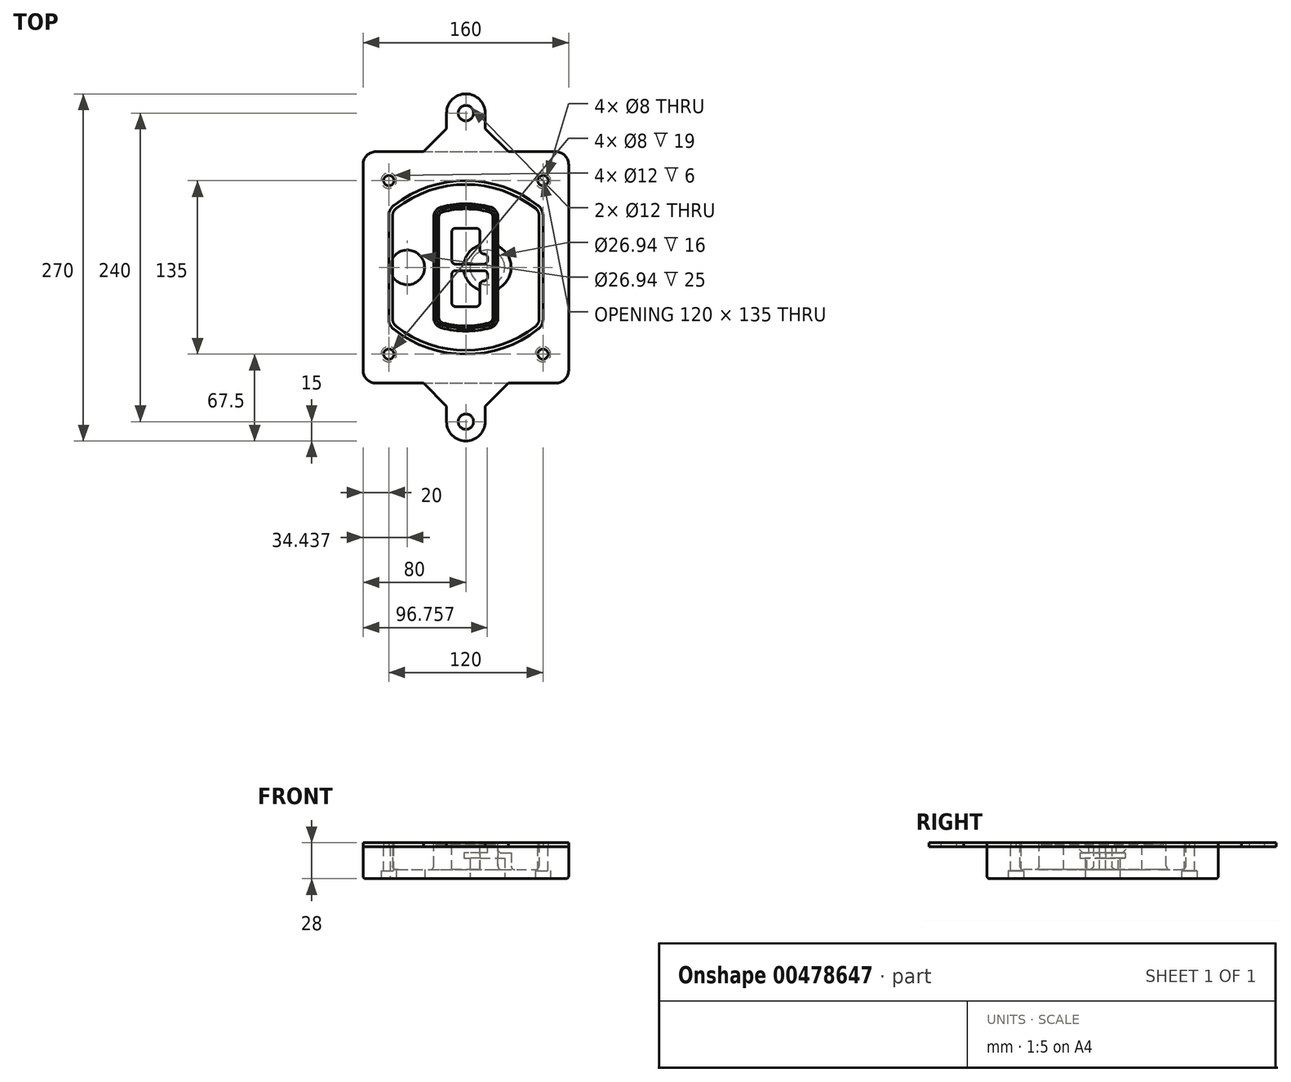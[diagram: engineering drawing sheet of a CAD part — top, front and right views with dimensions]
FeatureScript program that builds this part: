
annotation { "Feature Type Name" : "Feature", "Feature Type Description" : "" }
export const myFeature = defineFeature(function(context is Context, id is Id, definition is map)
    precondition{}
    {
        {
            var Q0;
            Q0=qCreatedBy(makeId("Top.planeOp"),FACE);
            var sketch = newSketch(context, id + "F0", { "sketchPlane" : qUnion([Q0])});
            skPoint(sketch, "E0.rect.middle", {"position": v(0, 0) * mm});
            skLineSegment(sketch, "E1.bottom", {"start": v(-70, -90) * mm, "end": v(70, -90) * mm});
            skLineSegment(sketch, "E1.top", {"start": v(-70, 90) * mm, "end": v(70, 90) * mm});
            skLineSegment(sketch, "E1.left", {"start": v(-80, -80) * mm, "end": v(-80, 80) * mm});
            skLineSegment(sketch, "E1.right", {"start": v(80, -80) * mm, "end": v(80, 80) * mm});
            skLineSegment(sketch, "E2", {"start": v(-80, 90) * mm, "end": v(80, -90) * mm, "construction": true});
            skLineSegment(sketch, "E3", {"start": v(80, 90) * mm, "end": v(-80, -90) * mm, "construction": true});
            skCircle(sketch, "E4", {"center": v(-60, 67.5) * mm, "radius": 4 * mm});
            skCircle(sketch, "E5", {"center": v(60, 67.5) * mm, "radius": 4 * mm});
            skCircle(sketch, "E6", {"center": v(60, -67.5) * mm, "radius": 4 * mm});
            skCircle(sketch, "E7", {"center": v(-60, -67.5) * mm, "radius": 4 * mm});
            skLineSegment(sketch, "E8", {"start": v(-60, 67.5) * mm, "end": v(60, 67.5) * mm, "construction": true});
            skLineSegment(sketch, "E9", {"start": v(60, 67.5) * mm, "end": v(60, -67.5) * mm, "construction": true});
            skLineSegment(sketch, "E10", {"start": v(60, -67.5) * mm, "end": v(-60, -67.5) * mm, "construction": true});
            skLineSegment(sketch, "E11", {"start": v(-60, -67.5) * mm, "end": v(-60, 67.5) * mm, "construction": true});
            skLineSegment(sketch, "E12", {"start": v(-60, 40.3) * mm, "end": v(-60, -40.3) * mm});
            skLineSegment(sketch, "E13", {"start": v(60, 40.3) * mm, "end": v(60, -40.3) * mm});
            skArc(sketch, "E14", {"start": v(56.15, 48.18) * mm, "mid": v(0, 67.5) * mm, "end": v(-56.15, 48.18) * mm});
            skArc(sketch, "E15", {"start": v(-56.15, -48.18) * mm, "mid": v(0, -67.5) * mm, "end": v(56.15, -48.18) * mm});
            skLineSegment(sketch, "E16", {"start": v(-60, 0) * mm, "end": v(60, 0) * mm, "construction": true});
            skPoint(sketch, "E17.visualSharp", {"position": v(-60, -45) * mm});
            skArc(sketch, "E17.filletArc", {"start": v(-60, -40.3) * mm, "mid": v(-58.99, -44.68) * mm, "end": v(-56.15, -48.18) * mm});
            skPoint(sketch, "E18.visualSharp", {"position": v(-60, 45) * mm});
            skArc(sketch, "E18.filletArc", {"start": v(-56.15, 48.18) * mm, "mid": v(-58.99, 44.68) * mm, "end": v(-60, 40.3) * mm});
            skPoint(sketch, "E19.visualSharp", {"position": v(60, 45) * mm});
            skArc(sketch, "E19.filletArc", {"start": v(60, 40.3) * mm, "mid": v(58.99, 44.68) * mm, "end": v(56.15, 48.18) * mm});
            skPoint(sketch, "E20.visualSharp", {"position": v(60, -45) * mm});
            skArc(sketch, "E20.filletArc", {"start": v(56.15, -48.18) * mm, "mid": v(58.99, -44.68) * mm, "end": v(60, -40.3) * mm});
            skPoint(sketch, "E21.visualSharp", {"position": v(-80, 90) * mm});
            skArc(sketch, "E21.filletArc", {"start": v(-70, 90) * mm, "mid": v(-77.07, 87.07) * mm, "end": v(-80, 80) * mm});
            skPoint(sketch, "E22.visualSharp", {"position": v(80, 90) * mm});
            skArc(sketch, "E22.filletArc", {"start": v(80, 80) * mm, "mid": v(77.07, 87.07) * mm, "end": v(70, 90) * mm});
            skPoint(sketch, "E23.visualSharp", {"position": v(80, -90) * mm});
            skArc(sketch, "E23.filletArc", {"start": v(70, -90) * mm, "mid": v(77.07, -87.07) * mm, "end": v(80, -80) * mm});
            skPoint(sketch, "E24.visualSharp", {"position": v(-80, -90) * mm});
            skArc(sketch, "E24.filletArc", {"start": v(-80, -80) * mm, "mid": v(-77.07, -87.07) * mm, "end": v(-70, -90) * mm});
            skArc(sketch, "E25.0", {"start": v(57, 40.3) * mm, "mid": v(56.3, 43.36) * mm, "end": v(54.3, 45.81) * mm});
            skLineSegment(sketch, "E25.1", {"start": v(57, 40.3) * mm, "end": v(57, -40.3) * mm});
            skArc(sketch, "E25.2", {"start": v(54.3, -45.81) * mm, "mid": v(56.3, -43.36) * mm, "end": v(57, -40.3) * mm});
            skArc(sketch, "E25.3", {"start": v(-54.3, -45.81) * mm, "mid": v(0, -64.5) * mm, "end": v(54.3, -45.81) * mm});
            skArc(sketch, "E25.4", {"start": v(-57, -40.3) * mm, "mid": v(-56.3, -43.36) * mm, "end": v(-54.3, -45.81) * mm});
            skArc(sketch, "E25.5", {"start": v(54.3, 45.81) * mm, "mid": v(0, 64.5) * mm, "end": v(-54.3, 45.81) * mm});
            skLineSegment(sketch, "E25.6", {"start": v(-57, 40.3) * mm, "end": v(-57, -40.3) * mm});
            skArc(sketch, "E25.7", {"start": v(-54.3, 45.81) * mm, "mid": v(-56.3, 43.36) * mm, "end": v(-57, 40.3) * mm});
            skArc(sketch, "E26.0", {"start": v(-58.62, 51.33) * mm, "mid": v(-62.58, 46.43) * mm, "end": v(-64, 40.3) * mm});
            skArc(sketch, "E26.1", {"start": v(58.62, 51.33) * mm, "mid": v(0, 71.5) * mm, "end": v(-58.62, 51.33) * mm});
            skArc(sketch, "E26.2", {"start": v(64, 40.3) * mm, "mid": v(62.58, 46.43) * mm, "end": v(58.62, 51.33) * mm});
            skLineSegment(sketch, "E26.3", {"start": v(64, 40.3) * mm, "end": v(64, -40.3) * mm});
            skArc(sketch, "E26.4", {"start": v(58.62, -51.33) * mm, "mid": v(62.58, -46.43) * mm, "end": v(64, -40.3) * mm});
            skLineSegment(sketch, "E26.5", {"start": v(-64, 40.3) * mm, "end": v(-64, -40.3) * mm});
            skArc(sketch, "E26.6", {"start": v(-58.62, -51.33) * mm, "mid": v(0, -71.5) * mm, "end": v(58.62, -51.33) * mm});
            skArc(sketch, "E26.7", {"start": v(-64, -40.3) * mm, "mid": v(-62.58, -46.43) * mm, "end": v(-58.62, -51.33) * mm});
            skSolve(sketch);
        }
        {
            var Q0;
            Q0=makeQuery(id+"F0.imprint","IMPRINT",FACE,{"disambiguationData":[TD([[makeQuery(id+"F0.imprint","IMPRINT",EDGE,{"derivedFrom":sQuery(id+"F0.wireOp",EDGE,"E1.bottom")}),1.0]])]});
            var Q1;
            Q1=makeQuery(id+"F0.imprint","IMPRINT",FACE,{"disambiguationData":[TD([[makeQuery(id+"F0.imprint","IMPRINT",EDGE,{"derivedFrom":sQuery(id+"F0.wireOp",EDGE,"E12")}),1.0]])]});
            var Q2;
            Q2=makeQuery(id+"F0.imprint","IMPRINT",FACE,{"disambiguationData":[TD([[makeQuery(id+"F0.imprint","IMPRINT",EDGE,{"derivedFrom":sQuery(id+"F0.wireOp",EDGE,"E25.0")}),1.0]])]});
            var Q3;
            Q3=makeQuery(id+"F0.imprint","IMPRINT",FACE,{"disambiguationData":[TD([[makeQuery(id+"F0.imprint","IMPRINT",EDGE,{"derivedFrom":sQuery(id+"F0.wireOp",EDGE,"E12")}),-1.0]])]});
            extrude(context, id + "F1", {"entities" : qUnion([Q0, Q1, Q2, Q3]), "oppositeDirection" : true, "depth" : 25 * mm});
        }
        {
            var Q0;
            Q0=makeQuery(id+"F0.imprint","IMPRINT",FACE,{"disambiguationData":[TD([[makeQuery(id+"F0.imprint","IMPRINT",EDGE,{"derivedFrom":sQuery(id+"F0.wireOp",EDGE,"E12")}),1.0]])]});
            extrude(context, id + "F2", {"entities" : qUnion([Q0]), "operationType" : NewBodyOperationType.ADD, "depth" : 3 * mm});
        }
        {
            var Q0;
            Q0=makeQuery(id+"F0.imprint","IMPRINT",FACE,{"disambiguationData":[TD([[makeQuery(id+"F0.imprint","IMPRINT",EDGE,{"derivedFrom":sQuery(id+"F0.wireOp",EDGE,"E25.0")}),1.0]])]});
            extrude(context, id + "F3", {"entities" : qUnion([Q0]), "operationType" : NewBodyOperationType.REMOVE, "oppositeDirection" : true, "depth" : 18 * mm});
        }
        {
            var Q0;
            Q0=makeQuery(id+"F2.opExtrude","CAP_FACE",FACE,{"disambiguationData":[OSD([sQuery(id+"F0.wireOp",EDGE,"E12"),sQuery(id+"F0.wireOp",EDGE,"E13"),sQuery(id+"F0.wireOp",EDGE,"E14"),sQuery(id+"F0.wireOp",EDGE,"E15"),sQuery(id+"F0.wireOp",EDGE,"E17.filletArc"),sQuery(id+"F0.wireOp",EDGE,"E18.filletArc"),sQuery(id+"F0.wireOp",EDGE,"E19.filletArc"),sQuery(id+"F0.wireOp",EDGE,"E20.filletArc"),sQuery(id+"F0.wireOp",EDGE,"E25.0"),sQuery(id+"F0.wireOp",EDGE,"E25.1"),sQuery(id+"F0.wireOp",EDGE,"E25.2"),sQuery(id+"F0.wireOp",EDGE,"E25.3"),sQuery(id+"F0.wireOp",EDGE,"E25.4"),sQuery(id+"F0.wireOp",EDGE,"E25.5"),sQuery(id+"F0.wireOp",EDGE,"E25.6"),sQuery(id+"F0.wireOp",EDGE,"E25.7")])],"isStart":false});
            var sketch = newSketch(context, id + "F4", { "sketchPlane" : qUnion([Q0])});
            skArc(sketch, "E27.0", {"start": v(-19.08, -46.97) * mm, "mid": v(0, -49.5) * mm, "end": v(19.08, -46.97) * mm});
            skArc(sketch, "E28.0", {"start": v(19.08, 46.97) * mm, "mid": v(0, 49.5) * mm, "end": v(-19.08, 46.97) * mm});
            skLineSegment(sketch, "E29", {"start": v(-25, 39.25) * mm, "end": v(-25, -39.25) * mm});
            skLineSegment(sketch, "E30", {"start": v(25, 39.25) * mm, "end": v(25, -39.25) * mm});
            skLineSegment(sketch, "E31", {"start": v(-25, 45.1) * mm, "end": v(25, 45.1) * mm, "construction": true});
            skLineSegment(sketch, "E32", {"start": v(-25, -45.1) * mm, "end": v(25, -45.1) * mm, "construction": true});
            skPoint(sketch, "E33.visualSharp", {"position": v(-25, 45.1) * mm});
            skArc(sketch, "E33.filletArc", {"start": v(-19.08, 46.97) * mm, "mid": v(-23.35, 44.11) * mm, "end": v(-25, 39.25) * mm});
            skPoint(sketch, "E34.visualSharp", {"position": v(25, 45.1) * mm});
            skArc(sketch, "E34.filletArc", {"start": v(25, 39.25) * mm, "mid": v(23.35, 44.11) * mm, "end": v(19.08, 46.97) * mm});
            skPoint(sketch, "E35.visualSharp", {"position": v(25, -45.1) * mm});
            skArc(sketch, "E35.filletArc", {"start": v(19.08, -46.97) * mm, "mid": v(23.35, -44.11) * mm, "end": v(25, -39.25) * mm});
            skPoint(sketch, "E36.visualSharp", {"position": v(-25, -45.1) * mm});
            skArc(sketch, "E36.filletArc", {"start": v(-25, -39.25) * mm, "mid": v(-23.35, -44.11) * mm, "end": v(-19.08, -46.97) * mm});
            skArc(sketch, "E37.0", {"start": v(54.3, 45.81) * mm, "mid": v(0, 64.5) * mm, "end": v(-54.3, 45.81) * mm});
            skArc(sketch, "E37.1", {"start": v(-54.3, 45.81) * mm, "mid": v(-56.3, 43.36) * mm, "end": v(-57, 40.3) * mm});
            skLineSegment(sketch, "E37.2", {"start": v(-57, 40.3) * mm, "end": v(-57, -40.3) * mm});
            skArc(sketch, "E37.3", {"start": v(-57, -40.3) * mm, "mid": v(-56.3, -43.36) * mm, "end": v(-54.3, -45.81) * mm});
            skArc(sketch, "E37.4", {"start": v(-54.3, -45.81) * mm, "mid": v(0, -64.5) * mm, "end": v(54.3, -45.81) * mm});
            skArc(sketch, "E37.5", {"start": v(54.3, -45.81) * mm, "mid": v(56.3, -43.36) * mm, "end": v(57, -40.3) * mm});
            skLineSegment(sketch, "E37.6", {"start": v(57, 40.3) * mm, "end": v(57, -40.3) * mm});
            skArc(sketch, "E37.7", {"start": v(57, 40.3) * mm, "mid": v(56.3, 43.36) * mm, "end": v(54.3, 45.81) * mm});
            skLineSegment(sketch, "E38.0", {"start": v(23, 39.25) * mm, "end": v(23, -39.25) * mm});
            skArc(sketch, "E38.1", {"start": v(18.56, -45.04) * mm, "mid": v(21.76, -42.9) * mm, "end": v(23, -39.25) * mm});
            skArc(sketch, "E38.2", {"start": v(-18.56, -45.04) * mm, "mid": v(0, -47.5) * mm, "end": v(18.56, -45.04) * mm});
            skArc(sketch, "E38.3", {"start": v(-23, -39.25) * mm, "mid": v(-21.76, -42.9) * mm, "end": v(-18.56, -45.04) * mm});
            skLineSegment(sketch, "E38.4", {"start": v(-23, 39.25) * mm, "end": v(-23, -39.25) * mm});
            skArc(sketch, "E38.5", {"start": v(23, 39.25) * mm, "mid": v(21.76, 42.9) * mm, "end": v(18.56, 45.04) * mm});
            skArc(sketch, "E38.6", {"start": v(-18.56, 45.04) * mm, "mid": v(-21.76, 42.9) * mm, "end": v(-23, 39.25) * mm});
            skArc(sketch, "E38.7", {"start": v(18.56, 45.04) * mm, "mid": v(0, 47.5) * mm, "end": v(-18.56, 45.04) * mm});
            skArc(sketch, "E39.0", {"start": v(21, 39.25) * mm, "mid": v(20.18, 41.68) * mm, "end": v(18.04, 43.1) * mm});
            skLineSegment(sketch, "E39.1", {"start": v(21, 39.25) * mm, "end": v(21, -39.25) * mm});
            skArc(sketch, "E39.2", {"start": v(18.04, -43.1) * mm, "mid": v(20.18, -41.68) * mm, "end": v(21, -39.25) * mm});
            skArc(sketch, "E39.3", {"start": v(-18.04, -43.1) * mm, "mid": v(0, -45.5) * mm, "end": v(18.04, -43.1) * mm});
            skArc(sketch, "E39.4", {"start": v(-21, -39.25) * mm, "mid": v(-20.18, -41.68) * mm, "end": v(-18.04, -43.1) * mm});
            skArc(sketch, "E39.5", {"start": v(18.04, 43.1) * mm, "mid": v(0, 45.5) * mm, "end": v(-18.04, 43.1) * mm});
            skLineSegment(sketch, "E39.6", {"start": v(-21, 39.25) * mm, "end": v(-21, -39.25) * mm});
            skArc(sketch, "E39.7", {"start": v(-18.04, 43.1) * mm, "mid": v(-20.18, 41.68) * mm, "end": v(-21, 39.25) * mm});
            skLineSegment(sketch, "E40", {"start": v(-25, 0) * mm, "end": v(25, 0) * mm, "construction": true});
            skLineSegment(sketch, "E41", {"start": v(-11, 5.5) * mm, "end": v(-11, 27.5) * mm});
            skLineSegment(sketch, "E42", {"start": v(-8, 30.5) * mm, "end": v(8, 30.5) * mm});
            skLineSegment(sketch, "E43", {"start": v(11, 27.5) * mm, "end": v(11, 13.5) * mm});
            skLineSegment(sketch, "E44", {"start": v(14, 10.5) * mm, "end": v(14, 10.5) * mm});
            skLineSegment(sketch, "E45", {"start": v(17, 7.5) * mm, "end": v(17, 5.5) * mm});
            skLineSegment(sketch, "E46", {"start": v(14, 2.5) * mm, "end": v(-8, 2.5) * mm});
            skPoint(sketch, "E47.visualSharp", {"position": v(-11, 30.5) * mm});
            skArc(sketch, "E47.filletArc", {"start": v(-8, 30.5) * mm, "mid": v(-10.12, 29.62) * mm, "end": v(-11, 27.5) * mm});
            skPoint(sketch, "E48.visualSharp", {"position": v(11, 30.5) * mm});
            skArc(sketch, "E48.filletArc", {"start": v(11, 27.5) * mm, "mid": v(10.12, 29.62) * mm, "end": v(8, 30.5) * mm});
            skPoint(sketch, "E49.visualSharp", {"position": v(11, 10.5) * mm});
            skArc(sketch, "E49.filletArc", {"start": v(11, 13.5) * mm, "mid": v(11.88, 11.38) * mm, "end": v(14, 10.5) * mm});
            skPoint(sketch, "E50.visualSharp", {"position": v(17, 10.5) * mm});
            skArc(sketch, "E50.filletArc", {"start": v(17, 7.5) * mm, "mid": v(16.12, 9.62) * mm, "end": v(14, 10.5) * mm});
            skPoint(sketch, "E51.visualSharp", {"position": v(17, 2.5) * mm});
            skArc(sketch, "E51.filletArc", {"start": v(14, 2.5) * mm, "mid": v(16.12, 3.38) * mm, "end": v(17, 5.5) * mm});
            skPoint(sketch, "E52.visualSharp", {"position": v(-11, 2.5) * mm});
            skArc(sketch, "E52.filletArc", {"start": v(-11, 5.5) * mm, "mid": v(-10.12, 3.38) * mm, "end": v(-8, 2.5) * mm});
            skLineSegment(sketch, "E53.0.MirrorCS", {"start": v(14, -2.5) * mm, "end": v(-8, -2.5) * mm});
            skArc(sketch, "E54.0.MirrorCS", {"start": v(-11, -5.5) * mm, "mid": v(-10.12, -3.38) * mm, "end": v(-8, -2.5) * mm});
            skLineSegment(sketch, "E55.0.MirrorCS", {"start": v(-11, -5.5) * mm, "end": v(-11, -27.5) * mm});
            skArc(sketch, "E56.0.MirrorCS", {"start": v(-8, -30.5) * mm, "mid": v(-10.12, -29.62) * mm, "end": v(-11, -27.5) * mm});
            skLineSegment(sketch, "E57.0.MirrorCS", {"start": v(-8, -30.5) * mm, "end": v(8, -30.5) * mm});
            skArc(sketch, "E58.0.MirrorCS", {"start": v(11, -27.5) * mm, "mid": v(10.12, -29.62) * mm, "end": v(8, -30.5) * mm});
            skLineSegment(sketch, "E59.0.MirrorCS", {"start": v(11, -27.5) * mm, "end": v(11, -13.5) * mm});
            skArc(sketch, "E60.0.MirrorCS", {"start": v(11, -13.5) * mm, "mid": v(11.88, -11.38) * mm, "end": v(14, -10.5) * mm});
            skArc(sketch, "E61.0.MirrorCS", {"start": v(17, -7.5) * mm, "mid": v(16.12, -9.62) * mm, "end": v(14, -10.5) * mm});
            skLineSegment(sketch, "E62.0.MirrorCS", {"start": v(17, -7.5) * mm, "end": v(17, -5.5) * mm});
            skArc(sketch, "E63.0.MirrorCS", {"start": v(14, -2.5) * mm, "mid": v(16.12, -3.38) * mm, "end": v(17, -5.5) * mm});
            skSolve(sketch);
        }
        {
            var Q0;
            Q0=makeQuery(id+"F4.imprint","IMPRINT",FACE,{"disambiguationData":[TD([[makeQuery(id+"F4.imprint","IMPRINT",EDGE,{"derivedFrom":sQuery(id+"F4.wireOp",EDGE,"E27.0")}),1.0]])]});
            var Q1;
            Q1=makeQuery(id+"F4.imprint","IMPRINT",FACE,{"disambiguationData":[TD([[makeQuery(id+"F4.imprint","IMPRINT",EDGE,{"derivedFrom":sQuery(id+"F4.wireOp",EDGE,"E38.0")}),-1.0]])]});
            var Q2;
            Q2=makeQuery(id+"F4.imprint","IMPRINT",FACE,{"disambiguationData":[TD([[makeQuery(id+"F4.imprint","IMPRINT",EDGE,{"derivedFrom":sQuery(id+"F4.wireOp",EDGE,"E39.0")}),1.0]])]});
            extrude(context, id + "F5", {"entities" : qUnion([Q0, Q1, Q2]), "operationType" : NewBodyOperationType.ADD, "endBound" : BoundingType.UP_TO_NEXT, "oppositeDirection" : true, "depth" : 25 * mm});
        }
        {
            var Q0;
            Q0=makeQuery(id+"F4.imprint","IMPRINT",FACE,{"disambiguationData":[TD([[makeQuery(id+"F4.imprint","IMPRINT",EDGE,{"derivedFrom":sQuery(id+"F4.wireOp",EDGE,"E38.0")}),-1.0]])]});
            extrude(context, id + "F6", {"entities" : qUnion([Q0]), "operationType" : NewBodyOperationType.REMOVE, "oppositeDirection" : true, "depth" : 2 * mm});
        }
        {
            var Q0;
            Q0=makeQuery(id+"F1.opExtrude","CAP_FACE",FACE,{"disambiguationData":[OSD([sQuery(id+"F0.wireOp",EDGE,"E1.bottom"),sQuery(id+"F0.wireOp",EDGE,"E1.top"),sQuery(id+"F0.wireOp",EDGE,"E1.left"),sQuery(id+"F0.wireOp",EDGE,"E1.right"),sQuery(id+"F0.wireOp",EDGE,"E4"),sQuery(id+"F0.wireOp",EDGE,"E5"),sQuery(id+"F0.wireOp",EDGE,"E6"),sQuery(id+"F0.wireOp",EDGE,"E7"),sQuery(id+"F0.wireOp",EDGE,"E21.filletArc"),sQuery(id+"F0.wireOp",EDGE,"E22.filletArc"),sQuery(id+"F0.wireOp",EDGE,"E23.filletArc"),sQuery(id+"F0.wireOp",EDGE,"E24.filletArc")])],"isStart":false});
            var sketch = newSketch(context, id + "F7", { "sketchPlane" : qUnion([Q0])});
            skCircle(sketch, "E64", {"center": v(16.76, 0) * mm, "radius": 13.47 * mm});
            skCircle(sketch, "E65", {"center": v(-45.56, 0) * mm, "radius": 13.47 * mm});
            skLineSegment(sketch, "E66", {"start": v(80, 0) * mm, "end": v(-80, 0) * mm});
            skCircle(sketch, "E67", {"center": v(16.76, 0) * mm, "radius": 18.47 * mm});
            skCircle(sketch, "E68", {"center": v(60, -67.5) * mm, "radius": 6 * mm});
            skCircle(sketch, "E69", {"center": v(-60, -67.5) * mm, "radius": 6 * mm});
            skCircle(sketch, "E70", {"center": v(-60, 67.5) * mm, "radius": 6 * mm});
            skCircle(sketch, "E71", {"center": v(60, 67.5) * mm, "radius": 6 * mm});
            skSolve(sketch);
        }
        {
            var Q0;
            {var subQ1=sQuery(id+"F7.wireOp",EDGE,"E66");var subQ4=sQuery(id+"F7.wireOp",EDGE,"E64");var subQ6=makeQuery(id+"F7.imprint","INTERSECT",VERTEX,{"disambiguationData":[OD(0.0)],"derivedFrom":[subQ4,subQ1]});Q0=makeQuery(id+"F7.imprint","IMPRINT",FACE,{"disambiguationData":[TD([[makeQuery(id+"F7.imprint","IMPRINT",EDGE,{"disambiguationData":[TD([[subQ6,-1.0]])],"derivedFrom":subQ4}),-1.0]])]});}
            var Q1;
            {var subQ0=sQuery(id+"F7.wireOp",EDGE,"E66");var subQ1=sQuery(id+"F7.wireOp",EDGE,"E64");var subQ3=makeQuery(id+"F7.imprint","INTERSECT",VERTEX,{"disambiguationData":[OD(0.0)],"derivedFrom":[subQ1,subQ0]});Q1=makeQuery(id+"F7.imprint","IMPRINT",FACE,{"disambiguationData":[TD([[makeQuery(id+"F7.imprint","IMPRINT",EDGE,{"disambiguationData":[TD([[subQ3,-1.0]])],"derivedFrom":subQ1}),1.0]])]});}
            var Q2;
            {var subQ0=sQuery(id+"F7.wireOp",EDGE,"E66");var subQ1=sQuery(id+"F7.wireOp",EDGE,"E64");var subQ3=makeQuery(id+"F7.imprint","INTERSECT",VERTEX,{"disambiguationData":[OD(0.0)],"derivedFrom":[subQ1,subQ0]});Q2=makeQuery(id+"F7.imprint","IMPRINT",FACE,{"disambiguationData":[TD([[makeQuery(id+"F7.imprint","IMPRINT",EDGE,{"disambiguationData":[TD([[subQ3,1.0]])],"derivedFrom":subQ1}),1.0]])]});}
            var Q3;
            {var subQ1=sQuery(id+"F7.wireOp",EDGE,"E66");var subQ4=sQuery(id+"F7.wireOp",EDGE,"E64");var subQ6=makeQuery(id+"F7.imprint","INTERSECT",VERTEX,{"disambiguationData":[OD(0.0)],"derivedFrom":[subQ4,subQ1]});Q3=makeQuery(id+"F7.imprint","IMPRINT",FACE,{"disambiguationData":[TD([[makeQuery(id+"F7.imprint","IMPRINT",EDGE,{"disambiguationData":[TD([[subQ6,1.0]])],"derivedFrom":subQ4}),-1.0]])]});}
            extrude(context, id + "F8", {"entities" : qUnion([Q0, Q1, Q2, Q3]), "operationType" : NewBodyOperationType.ADD, "oppositeDirection" : true, "depth" : 20 * mm});
        }
        {
            var Q0;
            {var subQ0=sQuery(id+"F7.wireOp",EDGE,"E66");var subQ1=sQuery(id+"F7.wireOp",EDGE,"E64");var subQ3=makeQuery(id+"F7.imprint","INTERSECT",VERTEX,{"disambiguationData":[OD(0.0)],"derivedFrom":[subQ1,subQ0]});Q0=makeQuery(id+"F7.imprint","IMPRINT",FACE,{"disambiguationData":[TD([[makeQuery(id+"F7.imprint","IMPRINT",EDGE,{"disambiguationData":[TD([[subQ3,-1.0]])],"derivedFrom":subQ1}),1.0]])]});}
            var Q1;
            {var subQ0=sQuery(id+"F7.wireOp",EDGE,"E66");var subQ1=sQuery(id+"F7.wireOp",EDGE,"E64");var subQ3=makeQuery(id+"F7.imprint","INTERSECT",VERTEX,{"disambiguationData":[OD(0.0)],"derivedFrom":[subQ1,subQ0]});Q1=makeQuery(id+"F7.imprint","IMPRINT",FACE,{"disambiguationData":[TD([[makeQuery(id+"F7.imprint","IMPRINT",EDGE,{"disambiguationData":[TD([[subQ3,1.0]])],"derivedFrom":subQ1}),1.0]])]});}
            extrude(context, id + "F9", {"entities" : qUnion([Q0, Q1]), "operationType" : NewBodyOperationType.REMOVE, "oppositeDirection" : true, "depth" : 16 * mm});
        }
        {
            var Q0;
            {var subQ0=sQuery(id+"F7.wireOp",EDGE,"E66");var subQ1=sQuery(id+"F7.wireOp",EDGE,"E65");var subQ3=makeQuery(id+"F7.imprint","INTERSECT",VERTEX,{"disambiguationData":[OD(0.0)],"derivedFrom":[subQ1,subQ0]});Q0=makeQuery(id+"F7.imprint","IMPRINT",FACE,{"disambiguationData":[TD([[makeQuery(id+"F7.imprint","IMPRINT",EDGE,{"disambiguationData":[TD([[subQ3,-1.0]])],"derivedFrom":subQ1}),1.0]])]});}
            var Q1;
            {var subQ0=sQuery(id+"F7.wireOp",EDGE,"E66");var subQ1=sQuery(id+"F7.wireOp",EDGE,"E65");var subQ3=makeQuery(id+"F7.imprint","INTERSECT",VERTEX,{"disambiguationData":[OD(0.0)],"derivedFrom":[subQ1,subQ0]});Q1=makeQuery(id+"F7.imprint","IMPRINT",FACE,{"disambiguationData":[TD([[makeQuery(id+"F7.imprint","IMPRINT",EDGE,{"disambiguationData":[TD([[subQ3,1.0]])],"derivedFrom":subQ1}),1.0]])]});}
            extrude(context, id + "F10", {"entities" : qUnion([Q0, Q1]), "operationType" : NewBodyOperationType.REMOVE, "oppositeDirection" : true, "depth" : 25 * mm});
        }
        {
            var Q0;
            Q0=makeQuery(id+"F7.imprint","IMPRINT",FACE,{"disambiguationData":[TD([[makeQuery(id+"F7.imprint","IMPRINT",EDGE,{"derivedFrom":sQuery(id+"F7.wireOp",EDGE,"E68")}),1.0]])]});
            var Q1;
            Q1=makeQuery(id+"F7.imprint","IMPRINT",FACE,{"disambiguationData":[TD([[makeQuery(id+"F7.imprint","IMPRINT",EDGE,{"derivedFrom":makeQuery(id+"F1.opExtrude","CAP_EDGE",EDGE,{"disambiguationData":[OSD([sQuery(id+"F0.wireOp",EDGE,"E5")])],"isStart":false})}),-1.0]])]});
            var Q2;
            Q2=makeQuery(id+"F7.imprint","IMPRINT",FACE,{"disambiguationData":[TD([[makeQuery(id+"F7.imprint","IMPRINT",EDGE,{"derivedFrom":sQuery(id+"F7.wireOp",EDGE,"E69")}),1.0]])]});
            var Q3;
            Q3=makeQuery(id+"F7.imprint","IMPRINT",FACE,{"disambiguationData":[TD([[makeQuery(id+"F7.imprint","IMPRINT",EDGE,{"derivedFrom":makeQuery(id+"F1.opExtrude","CAP_EDGE",EDGE,{"disambiguationData":[OSD([sQuery(id+"F0.wireOp",EDGE,"E4")])],"isStart":false})}),-1.0]])]});
            var Q4;
            Q4=makeQuery(id+"F7.imprint","IMPRINT",FACE,{"disambiguationData":[TD([[makeQuery(id+"F7.imprint","IMPRINT",EDGE,{"derivedFrom":sQuery(id+"F7.wireOp",EDGE,"E70")}),1.0]])]});
            var Q5;
            Q5=makeQuery(id+"F7.imprint","IMPRINT",FACE,{"disambiguationData":[TD([[makeQuery(id+"F7.imprint","IMPRINT",EDGE,{"derivedFrom":makeQuery(id+"F1.opExtrude","CAP_EDGE",EDGE,{"disambiguationData":[OSD([sQuery(id+"F0.wireOp",EDGE,"E7")])],"isStart":false})}),-1.0]])]});
            var Q6;
            Q6=makeQuery(id+"F7.imprint","IMPRINT",FACE,{"disambiguationData":[TD([[makeQuery(id+"F7.imprint","IMPRINT",EDGE,{"derivedFrom":sQuery(id+"F7.wireOp",EDGE,"E71")}),1.0]])]});
            var Q7;
            Q7=makeQuery(id+"F7.imprint","IMPRINT",FACE,{"disambiguationData":[TD([[makeQuery(id+"F7.imprint","IMPRINT",EDGE,{"derivedFrom":makeQuery(id+"F1.opExtrude","CAP_EDGE",EDGE,{"disambiguationData":[OSD([sQuery(id+"F0.wireOp",EDGE,"E6")])],"isStart":false})}),-1.0]])]});
            extrude(context, id + "F11", {"entities" : qUnion([Q0, Q1, Q2, Q3, Q4, Q5, Q6, Q7]), "operationType" : NewBodyOperationType.REMOVE, "oppositeDirection" : true, "depth" : 6 * mm});
        }
        {
            var Q0;
            Q0=makeQuery(id+"F9.boolean.opBoolean","COPY",FACE,{"derivedFrom":makeQuery(id+"F9.opExtrude","CAP_FACE",FACE,{"disambiguationData":[OSD([sQuery(id+"F7.wireOp",EDGE,"E64")])],"isStart":false})});
            var sketch = newSketch(context, id + "F12", { "sketchPlane" : qUnion([Q0])});
            skArc(sketch, "E72.0", {"start": v(11, 17.55) * mm, "mid": v(2.57, 11.82) * mm, "end": v(-1.54, 2.5) * mm});
            skArc(sketch, "E72.1", {"start": v(-1.54, -2.5) * mm, "mid": v(2.57, -11.82) * mm, "end": v(11, -17.55) * mm});
            skLineSegment(sketch, "E73", {"start": v(-1.54, -2.5) * mm, "end": v(14, -2.5) * mm});
            skLineSegment(sketch, "E74.0", {"start": v(14, 2.5) * mm, "end": v(-1.54, 2.5) * mm});
            skArc(sketch, "E74.1", {"start": v(14, 2.5) * mm, "mid": v(16.12, 3.38) * mm, "end": v(17, 5.5) * mm});
            skLineSegment(sketch, "E74.2", {"start": v(17, 7.5) * mm, "end": v(17, 5.5) * mm});
            skArc(sketch, "E74.3", {"start": v(17, 7.5) * mm, "mid": v(16.12, 9.62) * mm, "end": v(14, 10.5) * mm});
            skArc(sketch, "E74.4", {"start": v(11, 13.5) * mm, "mid": v(11.88, 11.38) * mm, "end": v(14, 10.5) * mm});
            skLineSegment(sketch, "E74.5", {"start": v(11, 17.55) * mm, "end": v(11, 13.5) * mm});
            skLineSegment(sketch, "E74.7", {"start": v(14, -2.5) * mm, "end": v(-1.54, -2.5) * mm});
            skArc(sketch, "E74.8", {"start": v(14, -2.5) * mm, "mid": v(16.12, -3.38) * mm, "end": v(17, -5.5) * mm});
            skLineSegment(sketch, "E74.9", {"start": v(17, -7.5) * mm, "end": v(17, -5.5) * mm});
            skArc(sketch, "E74.10", {"start": v(17, -7.5) * mm, "mid": v(16.12, -9.62) * mm, "end": v(14, -10.5) * mm});
            skArc(sketch, "E74.11", {"start": v(11, -13.5) * mm, "mid": v(11.88, -11.38) * mm, "end": v(14, -10.5) * mm});
            skLineSegment(sketch, "E74.12", {"start": v(11, -17.55) * mm, "end": v(11, -13.5) * mm});
            skPoint(sketch, "E75.orphan", {"position": v(11, -27.5) * mm});
            skPoint(sketch, "E76.orphan", {"position": v(-8, -2.5) * mm});
            skPoint(sketch, "E77.orphan", {"position": v(-8, 2.5) * mm});
            skPoint(sketch, "E78.orphan", {"position": v(11, 27.5) * mm});
            skSolve(sketch);
        }
        {
            var Q0;
            {var subQ7=sQuery(id+"F12.wireOp",EDGE,"E72.0");var subQ14=sQuery(id+"F12.wireOp",EDGE,"E72.1");var subQ16=sQuery(id+"F12.wireOp",EDGE,"E74.1");var subQ18=sQuery(id+"F12.wireOp",EDGE,"E74.8");Q0=qUnion([makeQuery(id+"F12.imprint","IMPRINT",FACE,{"disambiguationData":[TD([[makeQuery(id+"F12.imprint","IMPRINT",EDGE,{"derivedFrom":subQ7}),1.0]])]}),makeQuery(id+"F12.imprint","IMPRINT",FACE,{"disambiguationData":[TD([[makeQuery(id+"F12.imprint","IMPRINT",EDGE,{"derivedFrom":subQ14}),1.0]])]}),makeQuery(id+"F12.imprint","IMPRINT",FACE,{"disambiguationData":[TD([[makeQuery(id+"F12.imprint","IMPRINT",EDGE,{"derivedFrom":subQ16}),1.0]])]}),makeQuery(id+"F12.imprint","IMPRINT",FACE,{"disambiguationData":[TD([[makeQuery(id+"F12.imprint","IMPRINT",EDGE,{"derivedFrom":subQ18}),-1.0]])]})]);}
            var Q1;
            Q1=makeQuery(id+"F5.boolean.opBoolean","SPLIT",FACE,{"disambiguationData":[TD([makeQuery(id+"F5.opExtrude","SWEPT_FACE",FACE,{"disambiguationData":[OSD([sQuery(id+"F4.wireOp",EDGE,"E41")])]})])],"derivedFrom":makeQuery(id+"F3.boolean.opBoolean","COPY",FACE,{"derivedFrom":makeQuery(id+"F3.opExtrude","CAP_FACE",FACE,{"disambiguationData":[OSD([sQuery(id+"F0.wireOp",EDGE,"E25.0"),sQuery(id+"F0.wireOp",EDGE,"E25.1"),sQuery(id+"F0.wireOp",EDGE,"E25.2"),sQuery(id+"F0.wireOp",EDGE,"E25.3"),sQuery(id+"F0.wireOp",EDGE,"E25.4"),sQuery(id+"F0.wireOp",EDGE,"E25.5"),sQuery(id+"F0.wireOp",EDGE,"E25.6"),sQuery(id+"F0.wireOp",EDGE,"E25.7")])],"isStart":false})})});
            extrude(context, id + "F13", {"entities" : qUnion([Q0]), "operationType" : NewBodyOperationType.REMOVE, "endBound" : BoundingType.UP_TO_SURFACE, "endBoundEntityFace" : qUnion([Q1]), "depth" : 25 * mm});
        }
        {
            var Q0;
            Q0=makeQuery(id+"F3.boolean.opBoolean","COPY",EDGE,{"derivedFrom":makeQuery(id+"F3.opExtrude","CAP_EDGE",EDGE,{"disambiguationData":[OSD([sQuery(id+"F0.wireOp",EDGE,"E25.6")])],"isStart":false})});
            var Q1;
            Q1=makeQuery(id+"F8.boolean.opBoolean","INTERSECT",EDGE,{"derivedFrom":[makeQuery(id+"F5.opExtrude","SWEPT_FACE",FACE,{"disambiguationData":[OSD([sQuery(id+"F4.wireOp",EDGE,"E30")])]}),makeQuery(id+"F8.opExtrude","CAP_FACE",FACE,{"disambiguationData":[OSD([sQuery(id+"F7.wireOp",EDGE,"E67")])],"isStart":false})]});
            var Q2;
            Q2=makeQuery(id+"F8.boolean.opBoolean","INTERSECT",EDGE,{"disambiguationData":[OD(1.0)],"derivedFrom":[makeQuery(id+"F5.opExtrude","SWEPT_FACE",FACE,{"disambiguationData":[OSD([sQuery(id+"F4.wireOp",EDGE,"E30")])]}),makeQuery(id+"F8.opExtrude","SWEPT_FACE",FACE,{"disambiguationData":[OSD([sQuery(id+"F7.wireOp",EDGE,"E67")])]})]});
            var Q3;
            {var subQ0=sQuery(id+"F4.wireOp",EDGE,"E30");Q3=makeQuery(id+"F8.boolean.opBoolean","SPLIT",EDGE,{"disambiguationData":[TD([makeQuery(id+"F5.opExtrude","SWEPT_FACE",FACE,{"disambiguationData":[OSD([sQuery(id+"F4.wireOp",EDGE,"E35.filletArc")])]})])],"derivedFrom":makeQuery(id+"F5.opExtrude","CAP_EDGE",EDGE,{"disambiguationData":[OSD([subQ0])],"isStart":false})});}
            var Q4;
            {var subQ0=sQuery(id+"F0.wireOp",EDGE,"E25.7");var subQ1=sQuery(id+"F0.wireOp",EDGE,"E25.1");var subQ2=sQuery(id+"F0.wireOp",EDGE,"E25.6");var subQ3=sQuery(id+"F0.wireOp",EDGE,"E25.5");var subQ4=sQuery(id+"F0.wireOp",EDGE,"E25.4");var subQ5=sQuery(id+"F0.wireOp",EDGE,"E25.0");var subQ6=sQuery(id+"F0.wireOp",EDGE,"E25.2");var subQ7=sQuery(id+"F0.wireOp",EDGE,"E25.3");Q4=makeQuery(id+"F8.boolean.opBoolean","INTERSECT",EDGE,{"derivedFrom":[makeQuery(id+"F5.boolean.opBoolean","SPLIT",FACE,{"disambiguationData":[TD([makeQuery(id+"F2.opExtrude","SWEPT_FACE",FACE,{"disambiguationData":[OSD([subQ5])]})])],"derivedFrom":makeQuery(id+"F3.boolean.opBoolean","COPY",FACE,{"derivedFrom":makeQuery(id+"F3.opExtrude","CAP_FACE",FACE,{"disambiguationData":[OSD([subQ5,subQ1,subQ6,subQ7,subQ4,subQ3,subQ2,subQ0])],"isStart":false})})}),makeQuery(id+"F8.opExtrude","SWEPT_FACE",FACE,{"disambiguationData":[OSD([sQuery(id+"F7.wireOp",EDGE,"E67")])]})]});}
            var Q5;
            Q5=makeQuery(id+"F8.boolean.opBoolean","INTERSECT",EDGE,{"disambiguationData":[OD(0.0)],"derivedFrom":[makeQuery(id+"F5.opExtrude","SWEPT_FACE",FACE,{"disambiguationData":[OSD([sQuery(id+"F4.wireOp",EDGE,"E30")])]}),makeQuery(id+"F8.opExtrude","SWEPT_FACE",FACE,{"disambiguationData":[OSD([sQuery(id+"F7.wireOp",EDGE,"E67")])]})]});
            fillet(context, id + "F14", {"entities" : qUnion([Q0, Q1, Q2, Q3, Q4, Q5]), "radius" : 3 * mm, "tangentPropagation" : true, "allowEdgeOverflow" : false});
        }
        {
            var Q0;
            Q0=makeQuery(id+"F1.opExtrude","CAP_EDGE",EDGE,{"disambiguationData":[OSD([sQuery(id+"F0.wireOp",EDGE,"E1.bottom")])],"isStart":false});
            fillet(context, id + "F15", {"entities" : qUnion([Q0]), "radius" : 2 * mm, "tangentPropagation" : true, "allowEdgeOverflow" : false});
        }
        {
            var Q0;
            {var subQ0=sQuery(id+"F0.wireOp",EDGE,"E21.filletArc");var subQ1=sQuery(id+"F0.wireOp",EDGE,"E7");var subQ2=sQuery(id+"F0.wireOp",EDGE,"E6");var subQ3=sQuery(id+"F0.wireOp",EDGE,"E5");var subQ4=sQuery(id+"F0.wireOp",EDGE,"E4");var subQ5=sQuery(id+"F0.wireOp",EDGE,"E22.filletArc");var subQ6=sQuery(id+"F0.wireOp",EDGE,"E1.bottom");var subQ7=sQuery(id+"F0.wireOp",EDGE,"E1.right");var subQ8=sQuery(id+"F0.wireOp",EDGE,"E1.top");var subQ9=sQuery(id+"F0.wireOp",EDGE,"E1.left");var subQ10=sQuery(id+"F0.wireOp",EDGE,"E23.filletArc");var subQ11=sQuery(id+"F0.wireOp",EDGE,"E24.filletArc");Q0=makeQuery(id+"F2.boolean.opBoolean","SPLIT",FACE,{"disambiguationData":[TD([makeQuery(id+"F1.opExtrude","SWEPT_FACE",FACE,{"disambiguationData":[OSD([subQ6])]})])],"derivedFrom":makeQuery(id+"F1.opExtrude","CAP_FACE",FACE,{"disambiguationData":[OSD([subQ6,subQ8,subQ9,subQ7,subQ4,subQ3,subQ2,subQ1,subQ0,subQ5,subQ10,subQ11])],"isStart":true})});}
            var sketch = newSketch(context, id + "F16", { "sketchPlane" : qUnion([Q0])});
            skLineSegment(sketch, "E79", {"start": v(0, 90) * mm, "end": v(0, 120) * mm, "construction": true});
            skCircle(sketch, "E80", {"center": v(0, 120) * mm, "radius": 6 * mm});
            skLineSegment(sketch, "E81", {"start": v(33, 90) * mm, "end": v(15, 108) * mm});
            skLineSegment(sketch, "E82", {"start": v(15, 108) * mm, "end": v(15, 120) * mm});
            skLineSegment(sketch, "E83", {"start": v(-33, 90) * mm, "end": v(-15, 108) * mm});
            skLineSegment(sketch, "E84", {"start": v(-15, 108) * mm, "end": v(-15, 120) * mm});
            skArc(sketch, "E85", {"start": v(-15, 120) * mm, "mid": v(0, 135) * mm, "end": v(15, 120) * mm});
            skLineSegment(sketch, "E86", {"start": v(80, 0) * mm, "end": v(-80, 0) * mm, "construction": true});
            skLineSegment(sketch, "E87.MirrorCS", {"start": v(-15, -108) * mm, "end": v(-15, -120) * mm});
            skLineSegment(sketch, "E88.MirrorCS", {"start": v(15, -108) * mm, "end": v(15, -120) * mm});
            skLineSegment(sketch, "E89.MirrorCS", {"start": v(33, -90) * mm, "end": v(15, -108) * mm});
            skLineSegment(sketch, "E90.MirrorCS", {"start": v(-33, -90) * mm, "end": v(-15, -108) * mm});
            skLineSegment(sketch, "E91.MirrorCS", {"start": v(0, -90) * mm, "end": v(0, -120) * mm, "construction": true});
            skCircle(sketch, "E92.MirrorC", {"center": v(0, -120) * mm, "radius": 6 * mm});
            skArc(sketch, "E93.MirrorCS", {"start": v(-15, -120) * mm, "mid": v(0, -135) * mm, "end": v(15, -120) * mm});
            skSolve(sketch);
        }
        {
            var Q0;
            Q0=makeQuery(id+"F16.imprint","IMPRINT",FACE,{"disambiguationData":[TD([[makeQuery(id+"F16.imprint","IMPRINT",EDGE,{"derivedFrom":sQuery(id+"F16.wireOp",EDGE,"E80")}),-1.0]])]});
            var Q1;
            Q1=makeQuery(id+"F16.imprint","IMPRINT",FACE,{"disambiguationData":[TD([[makeQuery(id+"F16.imprint","IMPRINT",EDGE,{"derivedFrom":sQuery(id+"F16.wireOp",EDGE,"E87.MirrorCS")}),1.0]])]});
            var Q2;
            Q2=makeQuery(id+"F16.imprint","IMPRINT",FACE,{"disambiguationData":[TD([[makeQuery(id+"F16.imprint","IMPRINT",EDGE,{"derivedFrom":makeQuery(id+"F1.opExtrude","CAP_EDGE",EDGE,{"disambiguationData":[OSD([sQuery(id+"F0.wireOp",EDGE,"E1.left")])],"isStart":true})}),-1.0]])]});
            var Q3;
            Q3=makeQuery(id+"F2.opExtrude","CAP_FACE",FACE,{"disambiguationData":[OSD([sQuery(id+"F0.wireOp",EDGE,"E12"),sQuery(id+"F0.wireOp",EDGE,"E13"),sQuery(id+"F0.wireOp",EDGE,"E14"),sQuery(id+"F0.wireOp",EDGE,"E15"),sQuery(id+"F0.wireOp",EDGE,"E17.filletArc"),sQuery(id+"F0.wireOp",EDGE,"E18.filletArc"),sQuery(id+"F0.wireOp",EDGE,"E19.filletArc"),sQuery(id+"F0.wireOp",EDGE,"E20.filletArc"),sQuery(id+"F0.wireOp",EDGE,"E25.0"),sQuery(id+"F0.wireOp",EDGE,"E25.1"),sQuery(id+"F0.wireOp",EDGE,"E25.2"),sQuery(id+"F0.wireOp",EDGE,"E25.3"),sQuery(id+"F0.wireOp",EDGE,"E25.4"),sQuery(id+"F0.wireOp",EDGE,"E25.5"),sQuery(id+"F0.wireOp",EDGE,"E25.6"),sQuery(id+"F0.wireOp",EDGE,"E25.7")])],"isStart":false});
            extrude(context, id + "F17", {"entities" : qUnion([Q0, Q1, Q2]), "endBound" : BoundingType.UP_TO_SURFACE, "endBoundEntityFace" : qUnion([Q3]), "depth" : 25 * mm});
        }
    });
